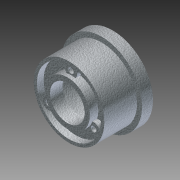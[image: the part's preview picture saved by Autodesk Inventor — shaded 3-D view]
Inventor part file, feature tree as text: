
AUTODESK INVENTOR PART (.ipt)
format: ipt  version: 2012 (Build 160160000, 160)  size: 173,056 bytes
history: native  units: in
note: dims shown in document units (in); Inventor stores cm internally (conversion verified against a paired STEP export)
features: extrude x8, sketch x3
ambient origin geometry x8: Origin, YZ Plane, XZ Plane, XY Plane, X Axis, Y Axis, Z Axis, Center Point
bodies: Solid1 (feature_tree)
feature tree (11):
  sketch  "Sketch1"  dims[d0=1.9275in d1=1.6875in]
  extrude  "Extrusion1"  Depth=1.6875in
  extrude  "Extrusion2"  Depth=1.071in
  extrude  "Extrusion3"  Depth=1.0825in TaperAngle=0.0deg
  extrude  "Extrusion4"  Depth=0.821in TaperAngle=0.0deg
  sketch  "Sketch2"  dims[d2=1.5375in d3=1.071in]
  extrude  "Extrusion5"  Depth=0.203in TaperAngle=0.0deg
  sketch  "Sketch3"  dims[d4=0.8275in d5=1.0825in d6=0.0in d7=0.821in d8=0.0in d9=0.203in d10=0.0in d11=0.04in d12=0.0in d13=0.1275in d14=0.2925in d15=0.625in d16=1.1811in d18=360.0deg d20=0.1155in d21=0.0in d22=1.82in d23=1.531in d24=0.7825in d25=0.0in d26=0.1075in d27=0.0in d28=0.1075in d29=0.0in]
  extrude  "Extrusion6"  Depth=0.04in TaperAngle=0.0deg
  extrude  "Extrusion7"  Depth=0.1275in
  extrude  "Extrusion8"  Depth=0.2925in
